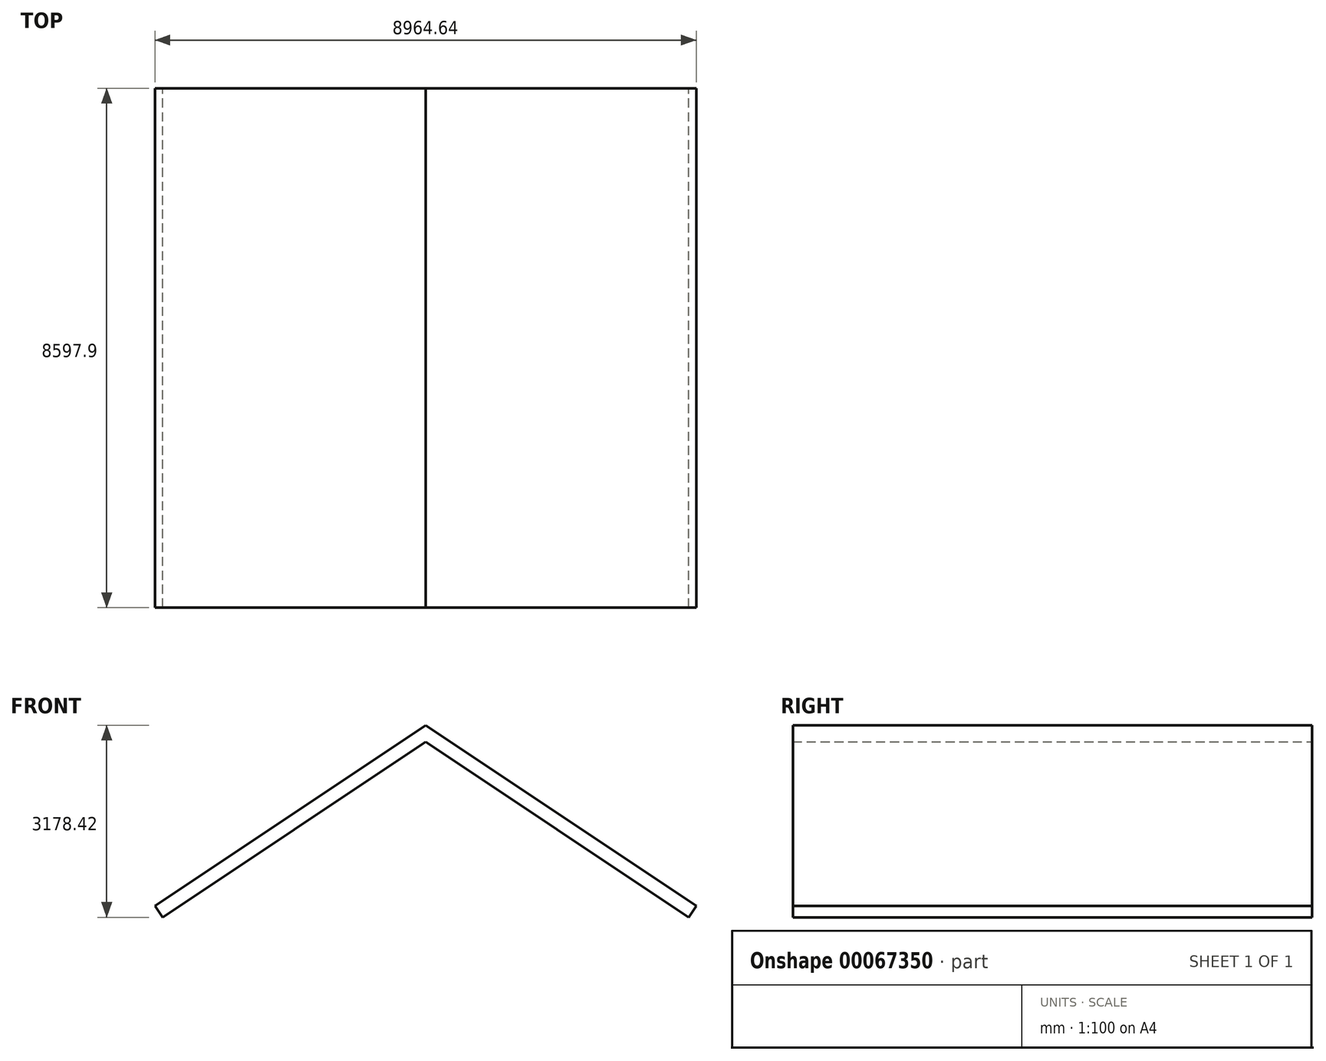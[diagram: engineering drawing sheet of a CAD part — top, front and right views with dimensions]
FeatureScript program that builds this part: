
annotation { "Feature Type Name" : "Feature", "Feature Type Description" : "" }
export const myFeature = defineFeature(function(context is Context, id is Id, definition is map)
    precondition{}
    {
        {
            var Q0;
            Q0=qCreatedBy(makeId("Front.planeOp"),FACE);
            var sketch = newSketch(context, id + "F0", { "sketchPlane" : qUnion([Q0])});
            skLineSegment(sketch, "E0", {"start": v(0, 0) * mm, "end": v(-4482.32, -2988.21) * mm});
            skLineSegment(sketch, "E1", {"start": v(0, 0) * mm, "end": v(4482.32, -2988.21) * mm});
            skLineSegment(sketch, "E2", {"start": v(-4482.32, -2988.21) * mm, "end": v(-4355.51, -3178.42) * mm});
            skLineSegment(sketch, "E3", {"start": v(-4355.51, -3178.42) * mm, "end": v(0, -274.74) * mm});
            skLineSegment(sketch, "E4", {"start": v(0, -274.74) * mm, "end": v(4355.51, -3178.42) * mm});
            skLineSegment(sketch, "E5", {"start": v(4355.51, -3178.42) * mm, "end": v(4482.32, -2988.21) * mm});
            skLineSegment(sketch, "E6", {"start": v(0, 0) * mm, "end": v(-304.8, 0) * mm, "construction": true});
            skLineSegment(sketch, "E7", {"start": v(-304.8, 0) * mm, "end": v(-304.8, -203.2) * mm, "construction": true});
            skLineSegment(sketch, "E8", {"start": v(-3975.1, -2650.07) * mm, "end": v(-3975.1, -2924.8) * mm, "construction": true});
            skLineSegment(sketch, "E9", {"start": v(3975.1, -2650.07) * mm, "end": v(3975.1, -2924.8) * mm, "construction": true});
            skLineSegment(sketch, "E10", {"start": v(0, 0) * mm, "end": v(0, -274.74) * mm, "construction": true});
            skSolve(sketch);
        }
        {
            var Q0;
            Q0=makeQuery(id+"F0.imprint","IMPRINT",FACE,{"disambiguationData":[TD([[makeQuery(id+"F0.imprint","IMPRINT",EDGE,{"derivedFrom":sQuery(id+"F0.wireOp",EDGE,"E0")}),1.0]])]});
            extrude(context, id + "F1", {"entities" : qUnion([Q0]), "endBound" : BoundingType.SYMMETRIC, "depth" : 8597.9 * mm});
        }
    });
